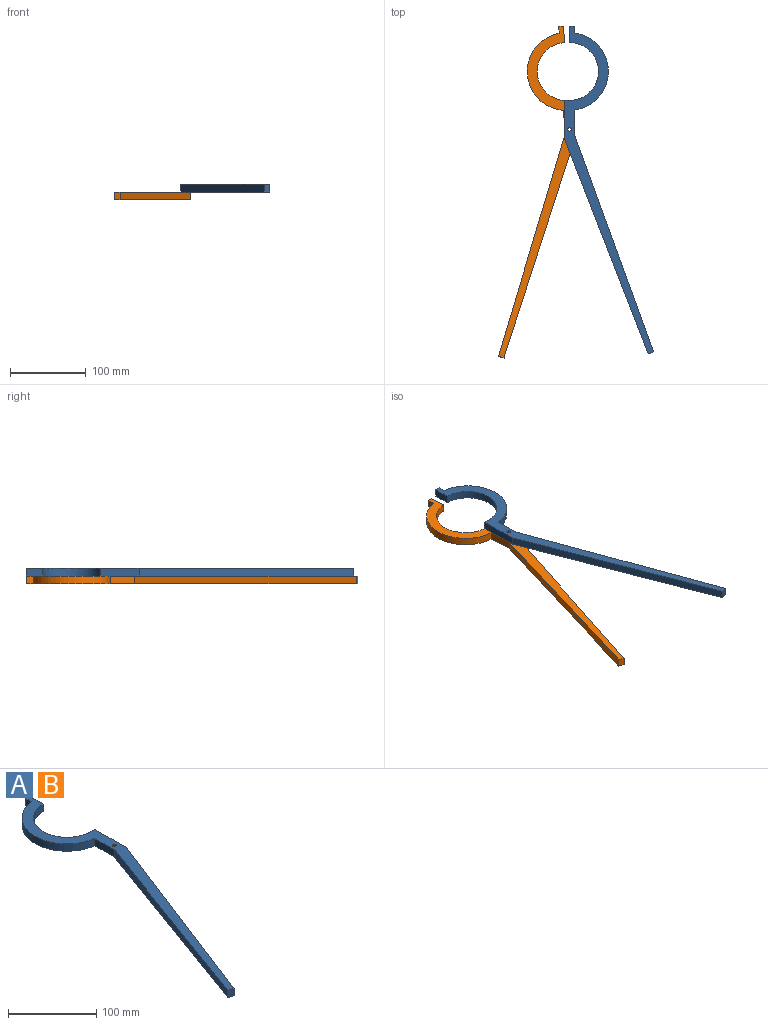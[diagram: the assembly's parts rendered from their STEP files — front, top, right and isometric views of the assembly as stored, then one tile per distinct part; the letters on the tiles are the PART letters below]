
ASSEMBLY  parts=2 mates=1
PART A: 14 faces, bbox 116.9x431.5x10.2 mm
  f0: cylinder r=38.1mm len=76.2mm, axis (0,0,-1), area 1216.1mm2, adj f1,f10,f11,f12
  f1: plane 21.74x10.16mm, normal (1,0,0), area 220.9mm2, adj f0,f2,f11,f12
  f2: plane 10.16x6.35mm, normal (0,1,0), area 64.5mm2, adj f1,f3,f11,f12
  f3: plane 10.16x9.04mm, normal (-1,0,0), area 91.9mm2, adj f2,f4,f11,f12
  f4: cylinder r=51.2mm len=101.6mm, axis (0,0,-1), area 1504.7mm2, adj f3,f5,f11,f12
  f5: plane 31.8x10.16mm, normal (-1,0,0), area 323.1mm2, adj f4,f6,f11,f12
  f6: plane 286.42x104.25mm, normal (-0.94,0.34,0), area 3096.8mm2, adj f5,f7,f11,f12
  f7: plane 10.16x7.16mm, normal (-0.34,-0.94,0), area 77.4mm2, adj f6,f8,f11,f12
  f8: plane 282.72x109.79mm, normal (0.93,-0.36,0), area 3081.4mm2, adj f7,f9,f11,f12
  f9: plane 50.8x10.16mm, normal (1,0,0), area 516.1mm2, adj f8,f10,f11,f12
  f10: plane 10.16x6.35mm, normal (0,1,0), area 64.5mm2, adj f0,f9,f11,f12
  f11: plane 431.47x116.95mm, normal (0,0,1), area 5702mm2, adj f0,f1,f2,f3,f4,f5,f6,f7
  f12: plane 431.47x116.95mm, normal (0,0,-1), area 5702mm2, adj f0,f1,f2,f3,f4,f5,f6,f7
  f13: cylinder r=2.25mm len=10.16mm, axis (0,0,1), area 143.5mm2, adj f11,f12
PART B: same geometry as A
PLACE A rot(axis=(0,1,0),180deg) t=(0,76.2,0)mm
PLACE B rot(axis=(0,0,1),3.3deg) t=(-4.39,76.07,-20.32)mm
MATE revolute A.f13 <-> B.f13  axis (0,0,-1) through (0,0,-10.16)mm
